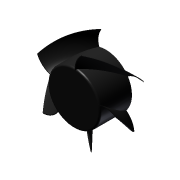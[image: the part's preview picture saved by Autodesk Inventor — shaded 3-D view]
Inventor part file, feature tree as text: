
AUTODESK INVENTOR PART (.ipt)
format: ipt  version: 2014 SP1 (Build 180222100, 222)  size: 241,152 bytes
history: native  units: mm (DEFAULTED — no unit token found)
features: sketch x2, extrude x1, fillet x1, other x1, helix x1, pattern_circular x1
ambient origin geometry x8: Origin, YZ Plane, XZ Plane, XY Plane, X Axis, Y Axis, Z Axis, Center Point
bodies: Solid1 (feature_tree)
feature tree (7):
  extrude  "Extrusion1"  Depth=0.79375mm
  fillet  "Fillet1"  Radius=0.3175mm
  sketch  "Sketch2"  dims[d5=0.698132mm d6=8.89mm d7=37.338mm d8=127.0mm d9=14.3002mm d10=1.5mm d11=0.0mm d12=90.0deg d13=90.0deg d14=0.0mm d15=0.0mm d16=50.0mm d18=360.0deg]
  other  "Work Axis1"
  helix  "Coil1"  [1 undecoded]
  pattern_circular  "Circular Pattern1"  [2 undecoded]
  sketch  "Sketch1"  dims[d0=14.3002mm d1=0.0mm d2=0.79375mm d3=0.3175mm d4=2.094086mm]
note: 3 required parameter values undecoded (feature->parameter linkage not recoverable at this tier; creation-order binding heuristic only, values carry confidence <= 0.55)
